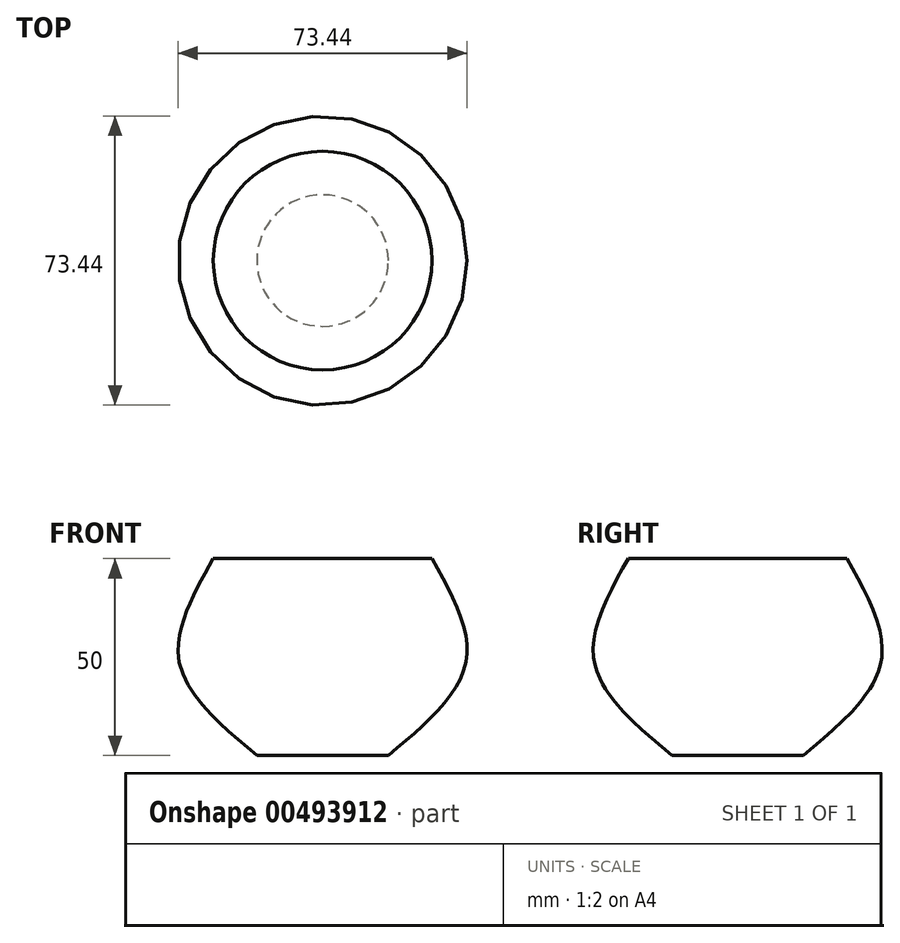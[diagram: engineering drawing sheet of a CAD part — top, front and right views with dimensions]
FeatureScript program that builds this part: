
annotation { "Feature Type Name" : "Feature", "Feature Type Description" : "" }
export const myFeature = defineFeature(function(context is Context, id is Id, definition is map)
    precondition{}
    {
        {
            var Q0;
            Q0=qCreatedBy(makeId("Top.planeOp"),FACE);
            cPlane(context, id + "F0", {"entities" : qUnion([Q0]), "cplaneType" : CPlaneType.OFFSET, "offset" : 25 * mm, "width" : 150 * mm, "height" : 150 * mm});
        }
        {
            var Q0;
            Q0=qCreatedBy(id+"F0.planeOp",FACE);
            cPlane(context, id + "F1", {"entities" : qUnion([Q0]), "cplaneType" : CPlaneType.OFFSET, "offset" : 25 * mm, "width" : 150 * mm, "height" : 150 * mm});
        }
        {
            var Q0;
            Q0=qCreatedBy(makeId("Top.planeOp"),FACE);
            var sketch = newSketch(context, id + "F2", { "sketchPlane" : qUnion([Q0])});
            skCircle(sketch, "E0", {"center": v(0, 0) * mm, "radius": 16.7 * mm});
            skSolve(sketch);
        }
        {
            var Q0;
            Q0=qCreatedBy(id+"F0.planeOp",FACE);
            var sketch = newSketch(context, id + "F3", { "sketchPlane" : qUnion([Q0])});
            skCircle(sketch, "E1", {"center": v(0, 0) * mm, "radius": 36.61 * mm});
            skSolve(sketch);
        }
        {
            var Q0;
            Q0=qCreatedBy(id+"F1.planeOp",FACE);
            var sketch = newSketch(context, id + "F4", { "sketchPlane" : qUnion([Q0])});
            skCircle(sketch, "E2", {"center": v(0, 0) * mm, "radius": 27.77 * mm});
            skSolve(sketch);
        }
        {
            var Q0;
            Q0=makeQuery(id+"F4.imprint","IMPRINT",FACE,{"disambiguationData":[TD([[makeQuery(id+"F4.imprint","IMPRINT",EDGE,{"derivedFrom":sQuery(id+"F4.wireOp",EDGE,"E2")}),1.0]])]});
            var Q1;
            Q1=makeQuery(id+"F3.imprint","IMPRINT",FACE,{"disambiguationData":[TD([[makeQuery(id+"F3.imprint","IMPRINT",EDGE,{"derivedFrom":sQuery(id+"F3.wireOp",EDGE,"E1")}),1.0]])]});
            var Q2;
            Q2=makeQuery(id+"F2.imprint","IMPRINT",FACE,{"disambiguationData":[TD([[makeQuery(id+"F2.imprint","IMPRINT",EDGE,{"derivedFrom":sQuery(id+"F2.wireOp",EDGE,"E0")}),1.0]])]});
            loft(context, id + "F5", {"sheetProfilesArray" : [{ "sheetProfileEntities" : qUnion([Q0]) }, { "sheetProfileEntities" : qUnion([Q1]) }, { "sheetProfileEntities" : qUnion([Q2]) }]});
        }
    });
